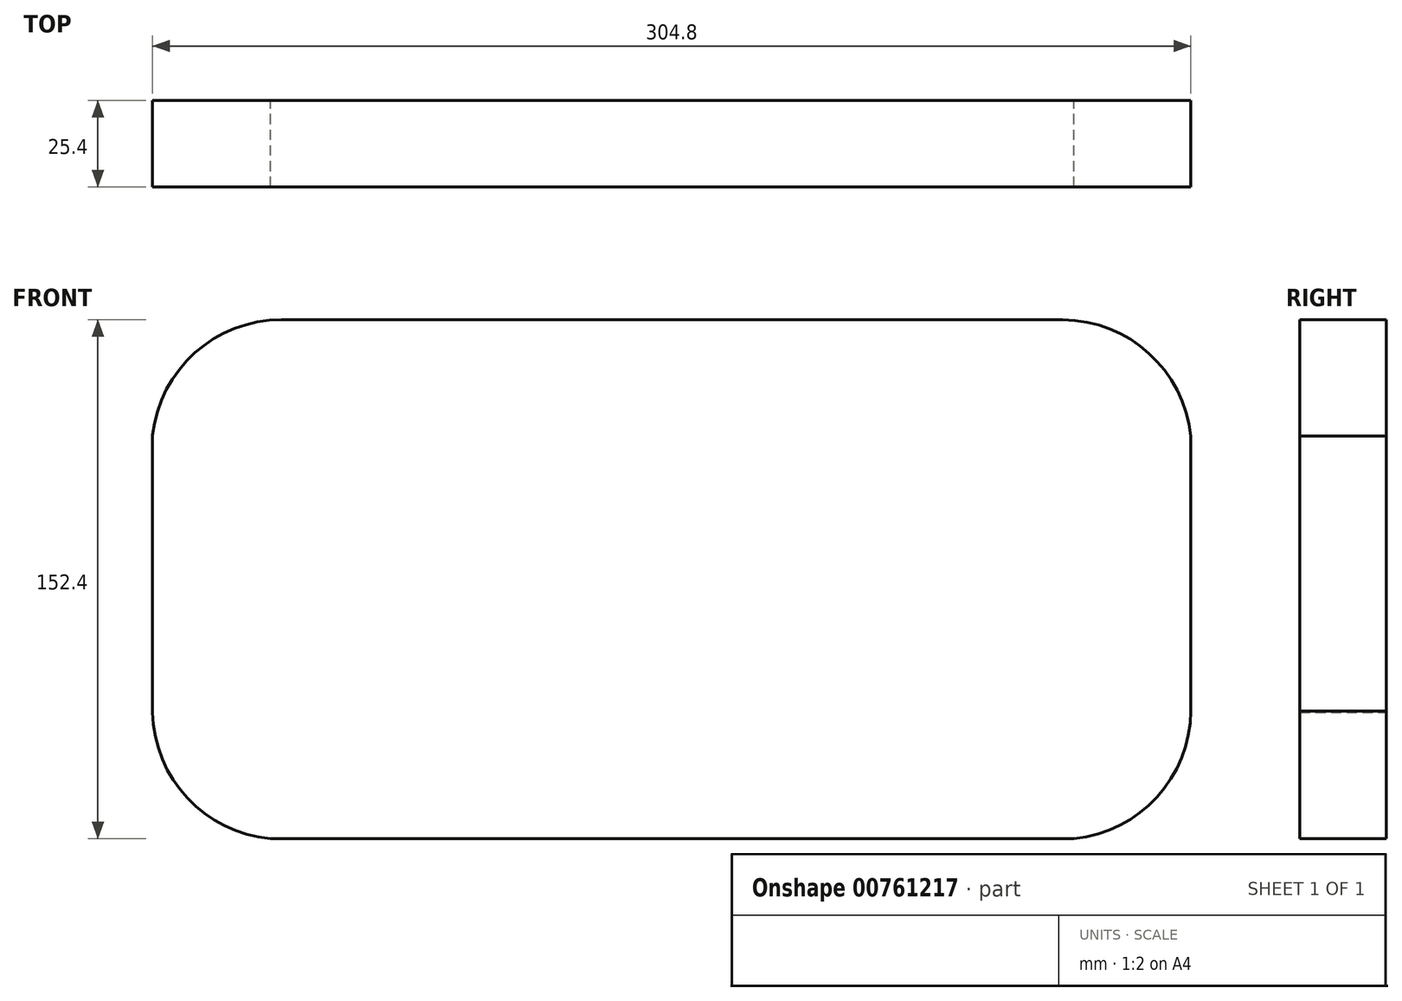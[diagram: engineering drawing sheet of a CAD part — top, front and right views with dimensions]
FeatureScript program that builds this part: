
annotation { "Feature Type Name" : "Feature", "Feature Type Description" : "" }
export const myFeature = defineFeature(function(context is Context, id is Id, definition is map)
    precondition{}
    {
        {
            var Q0;
            Q0=qCreatedBy(makeId("Front.planeOp"),FACE);
            var sketch = newSketch(context, id + "F0", { "sketchPlane" : qUnion([Q0])});
            skLineSegment(sketch, "E0.bottom", {"start": v(-120.92, 77.92) * mm, "end": v(108.38, 77.92) * mm});
            skLineSegment(sketch, "E0.top", {"start": v(-124.09, -74.48) * mm, "end": v(111.75, -74.48) * mm});
            skLineSegment(sketch, "E0.left", {"start": v(-158.78, 44.05) * mm, "end": v(-158.78, -37.38) * mm});
            skLineSegment(sketch, "E0.right", {"start": v(146.02, 43.8) * mm, "end": v(146.02, -36.99) * mm});
            skArc(sketch, "E1", {"start": v(-120.92, 77.92) * mm, "mid": v(-146.32, 68.21) * mm, "end": v(-158.78, 44.05) * mm});
            skArc(sketch, "E2", {"start": v(146.02, 35.84) * mm, "mid": v(136.52, 65.22) * mm, "end": v(108.38, 77.92) * mm});
            skArc(sketch, "E3", {"start": v(-158.78, -35.7) * mm, "mid": v(-146.72, -64.37) * mm, "end": v(-117.3, -74.48) * mm});
            skArc(sketch, "E4", {"start": v(104.1, -74.48) * mm, "mid": v(133.32, -64.97) * mm, "end": v(146.02, -36.99) * mm});
            skPoint(sketch, "E5.orphan", {"position": v(-158.78, 77.92) * mm});
            skPoint(sketch, "E6.orphan", {"position": v(-158.78, -74.48) * mm});
            skSolve(sketch);
        }
        {
            var Q0;
            {var subQ1=sQuery(id+"F0.wireOp",EDGE,"E0.bottom");Q0=makeQuery(id+"F0.imprint","IMPRINT",FACE,{"disambiguationData":[TD([[makeQuery(id+"F0.imprint","IMPRINT",EDGE,{"derivedFrom":subQ1}),-1.0]])]});}
            extrude(context, id + "F1", {"entities" : qUnion([Q0]), "depth" : 25.4 * mm, "offsetDistance" : 25.4 * mm});
        }
    });
